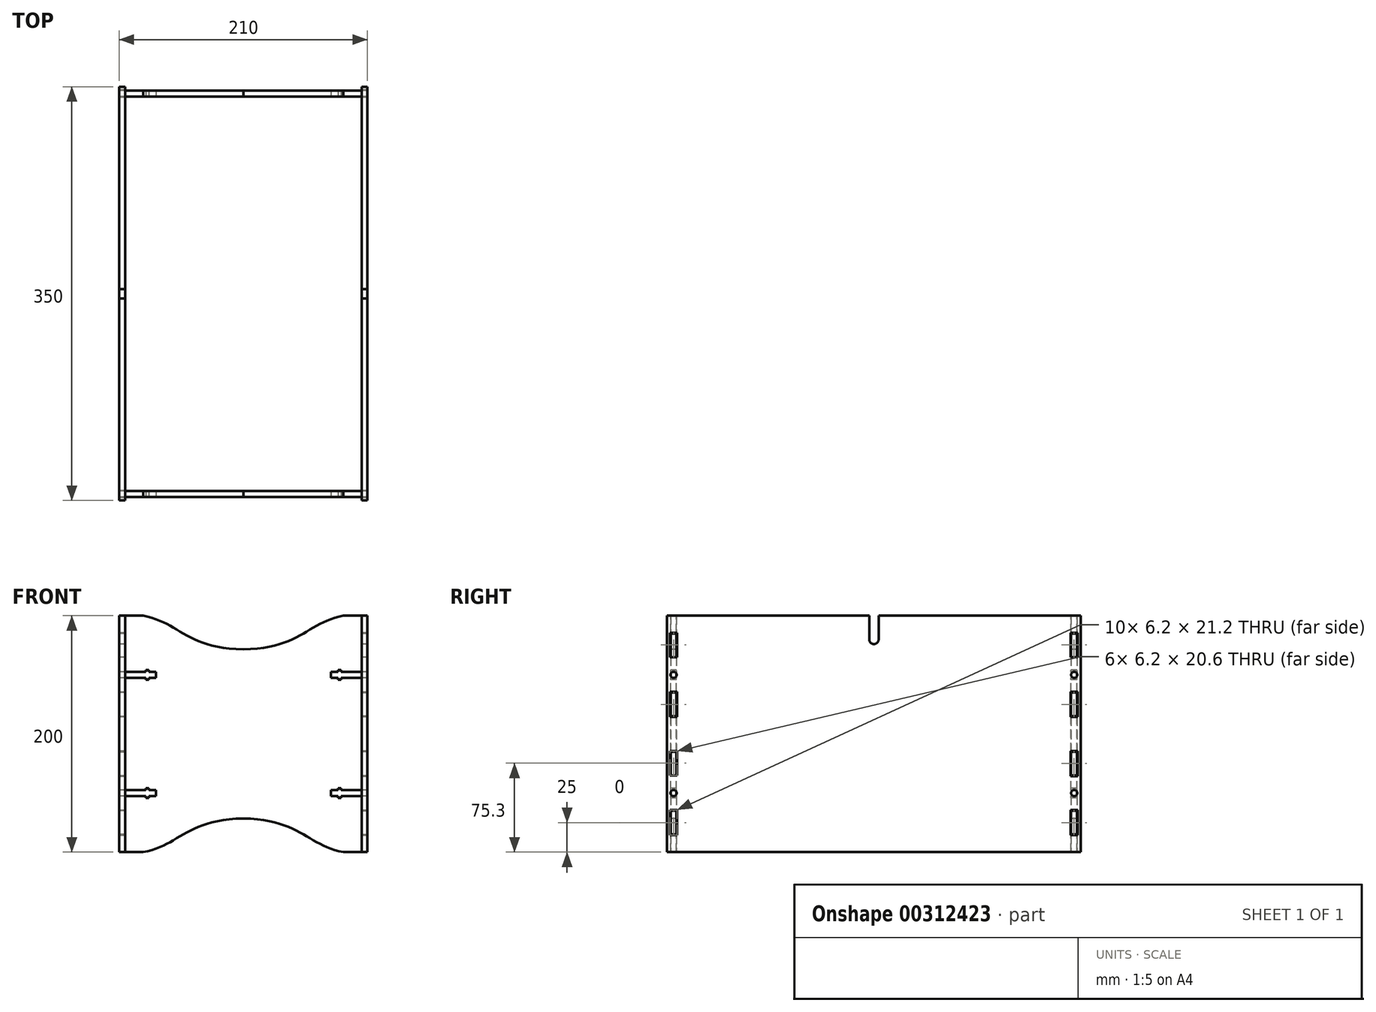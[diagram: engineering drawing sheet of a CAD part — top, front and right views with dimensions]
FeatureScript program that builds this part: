
annotation { "Feature Type Name" : "Feature", "Feature Type Description" : "" }
export const myFeature = defineFeature(function(context is Context, id is Id, definition is map)
    precondition{}
    {
        {
            var Q0;
            Q0=qCreatedBy(makeId("Right.planeOp"),FACE);
            var sketch = newSketch(context, id + "F0", { "sketchPlane" : qUnion([Q0])});
            skLineSegment(sketch, "E0.bottom", {"start": v(175, -100) * mm, "end": v(-175, -100) * mm});
            skLineSegment(sketch, "E0.top", {"start": v(175, 100) * mm, "end": v(4, 100) * mm});
            skLineSegment(sketch, "E0.left", {"start": v(175, -100) * mm, "end": v(175, 100) * mm});
            skLineSegment(sketch, "E0.right", {"start": v(-175, -100) * mm, "end": v(-175, 100) * mm});
            skPoint(sketch, "E0.middle", {"position": v(0, 0) * mm});
            skLineSegment(sketch, "E1", {"start": v(0, 80) * mm, "end": v(0, -100) * mm, "construction": true});
            skLineSegment(sketch, "E2", {"start": v(-175, 0) * mm, "end": v(175, 0) * mm, "construction": true});
            skLineSegment(sketch, "E3.trimOffspring", {"start": v(-4, 100) * mm, "end": v(-175, 100) * mm});
            skLineSegment(sketch, "E4", {"start": v(-172, 100) * mm, "end": v(-172, 85) * mm, "construction": true});
            skLineSegment(sketch, "E5", {"start": v(-166.8, 65) * mm, "end": v(-166.8, 35) * mm, "construction": true});
            skLineSegment(sketch, "E6.bottom", {"start": v(-172, 85) * mm, "end": v(-166.8, 85) * mm});
            skLineSegment(sketch, "E6.top", {"start": v(-172, 65) * mm, "end": v(-166.8, 65) * mm});
            skLineSegment(sketch, "E6.left", {"start": v(-172, 85) * mm, "end": v(-172, 65) * mm});
            skLineSegment(sketch, "E6.right", {"start": v(-166.8, 85) * mm, "end": v(-166.8, 65) * mm});
            skLineSegment(sketch, "E7.bottom", {"start": v(-172, 35) * mm, "end": v(-166.8, 35) * mm});
            skLineSegment(sketch, "E7.top", {"start": v(-172, 15) * mm, "end": v(-166.8, 15) * mm});
            skLineSegment(sketch, "E7.left", {"start": v(-172, 35) * mm, "end": v(-172, 15) * mm});
            skLineSegment(sketch, "E7.right", {"start": v(-166.8, 35) * mm, "end": v(-166.8, 15) * mm});
            skLineSegment(sketch, "E8", {"start": v(-169.4, 65) * mm, "end": v(-169.4, 35) * mm, "construction": true});
            skPoint(sketch, "E9", {"position": v(-169.4, 50) * mm});
            skCircle(sketch, "E10", {"center": v(-169.4, 50) * mm, "radius": 2.6 * mm});
            skLineSegment(sketch, "E11.MirrorCS", {"start": v(-172, -85) * mm, "end": v(-166.8, -85) * mm});
            skPoint(sketch, "E12.orphan", {"position": v(-166.8, 100) * mm});
            skLineSegment(sketch, "E13.trimOffspring", {"start": v(-172, 65) * mm, "end": v(-172, 35) * mm, "construction": true});
            skLineSegment(sketch, "E14.MirrorCS", {"start": v(-166.8, -85) * mm, "end": v(-166.8, -65) * mm});
            skLineSegment(sketch, "E15.MirrorCS", {"start": v(-172, -85) * mm, "end": v(-172, -65) * mm});
            skLineSegment(sketch, "E16.MirrorCS", {"start": v(-172, -65) * mm, "end": v(-166.8, -65) * mm});
            skCircle(sketch, "E17.MirrorC", {"center": v(-169.4, -50) * mm, "radius": 2.6 * mm});
            skLineSegment(sketch, "E18.MirrorCS", {"start": v(-172, -35) * mm, "end": v(-166.8, -35) * mm});
            skLineSegment(sketch, "E19.MirrorCS", {"start": v(-172, -15) * mm, "end": v(-166.8, -15) * mm});
            skLineSegment(sketch, "E20.trimOffspring", {"start": v(-172, 0) * mm, "end": v(-172, -15) * mm, "construction": true});
            skLineSegment(sketch, "E21.trimOffspring", {"start": v(-166.8, 0) * mm, "end": v(-166.8, -15) * mm, "construction": true});
            skLineSegment(sketch, "E22.MirrorCS", {"start": v(-172, -35) * mm, "end": v(-172, -15) * mm});
            skLineSegment(sketch, "E23.MirrorCS", {"start": v(-166.8, -35) * mm, "end": v(-166.8, -15) * mm});
            skLineSegment(sketch, "E24.trimOffspring", {"start": v(-172, -35) * mm, "end": v(-172, -65) * mm, "construction": true});
            skLineSegment(sketch, "E25.trimOffspring", {"start": v(-166.8, -35) * mm, "end": v(-166.8, -65) * mm, "construction": true});
            skLineSegment(sketch, "E26.trimOffspring", {"start": v(-166.8, -85) * mm, "end": v(-166.8, -100) * mm, "construction": true});
            skLineSegment(sketch, "E27.trimOffspring", {"start": v(-172, -85) * mm, "end": v(-172, -100) * mm, "construction": true});
            skLineSegment(sketch, "E28.MirrorCS", {"start": v(172, 85) * mm, "end": v(172, 65) * mm});
            skLineSegment(sketch, "E29.MirrorCS", {"start": v(166.8, 85) * mm, "end": v(166.8, 65) * mm});
            skLineSegment(sketch, "E30.MirrorCS", {"start": v(172, 85) * mm, "end": v(166.8, 85) * mm});
            skLineSegment(sketch, "E31.MirrorCS", {"start": v(172, 65) * mm, "end": v(166.8, 65) * mm});
            skCircle(sketch, "E32.MirrorC", {"center": v(169.4, 50) * mm, "radius": 2.6 * mm});
            skLineSegment(sketch, "E33.MirrorCS", {"start": v(172, 35) * mm, "end": v(166.8, 35) * mm});
            skLineSegment(sketch, "E34.MirrorCS", {"start": v(166.8, 35) * mm, "end": v(166.8, 15) * mm});
            skLineSegment(sketch, "E35.MirrorCS", {"start": v(172, 35) * mm, "end": v(172, 15) * mm});
            skLineSegment(sketch, "E36.MirrorCS", {"start": v(172, 15) * mm, "end": v(166.8, 15) * mm});
            skLineSegment(sketch, "E37.MirrorCS", {"start": v(172, -15) * mm, "end": v(166.8, -15) * mm});
            skLineSegment(sketch, "E38.MirrorCS", {"start": v(166.8, -35) * mm, "end": v(166.8, -15) * mm});
            skLineSegment(sketch, "E39.MirrorCS", {"start": v(172, -35) * mm, "end": v(172, -15) * mm});
            skLineSegment(sketch, "E40.MirrorCS", {"start": v(172, -35) * mm, "end": v(166.8, -35) * mm});
            skCircle(sketch, "E41.MirrorC", {"center": v(169.4, -50) * mm, "radius": 2.6 * mm});
            skLineSegment(sketch, "E42.MirrorCS", {"start": v(172, -65) * mm, "end": v(166.8, -65) * mm});
            skLineSegment(sketch, "E43.MirrorCS", {"start": v(172, -85) * mm, "end": v(166.8, -85) * mm});
            skLineSegment(sketch, "E44.MirrorCS", {"start": v(166.8, -85) * mm, "end": v(166.8, -65) * mm});
            skLineSegment(sketch, "E45.MirrorCS", {"start": v(172, -85) * mm, "end": v(172, -65) * mm});
            skLineSegment(sketch, "E46.left", {"start": v(4, 100) * mm, "end": v(4, 80) * mm});
            skLineSegment(sketch, "E46.right", {"start": v(-4, 100) * mm, "end": v(-4, 80) * mm});
            skArc(sketch, "E47", {"start": v(-4, 80) * mm, "mid": v(0, 76) * mm, "end": v(4, 80) * mm});
            skSolve(sketch);
        }
        {
            var Q0;
            Q0 = qSketchRegion(id + "F0", true);
            extrude(context, id + "F1", {"entities" : qUnion([Q0]), "depth" : 5 * mm});
        }
        {
            var Q0;
            Q0=makeQuery(id+"F1.opExtrude","SWEPT_FACE",FACE,{"disambiguationData":[OSD([sQuery(id+"F0.wireOp",EDGE,"E29.MirrorCS")])]});
            var sketch = newSketch(context, id + "F2", { "sketchPlane" : qUnion([Q0])});
            skPoint(sketch, "E48.0", {"position": v(-5, 100) * mm});
            skLineSegment(sketch, "E49.bottom", {"start": v(0, 100) * mm, "end": v(15.34, 100) * mm});
            skLineSegment(sketch, "E49.top", {"start": v(0, -100) * mm, "end": v(15.34, -100) * mm});
            skLineSegment(sketch, "E49.left", {"start": v(-5, 85) * mm, "end": v(-5, 65) * mm});
            skLineSegment(sketch, "E49.right", {"start": v(200, 100) * mm, "end": v(200, 52.6) * mm});
            skLineSegment(sketch, "E50.bottom", {"start": v(0, 52.6) * mm, "end": v(17.4, 52.6) * mm});
            skLineSegment(sketch, "E50.top", {"start": v(0, 47.4) * mm, "end": v(17.4, 47.4) * mm});
            skLineSegment(sketch, "E50.right", {"start": v(26, 52.6) * mm, "end": v(26, 47.4) * mm});
            skLineSegment(sketch, "E51.bottom", {"start": v(20, 45.95) * mm, "end": v(17.4, 45.95) * mm});
            skLineSegment(sketch, "E51.top", {"start": v(20, 54.05) * mm, "end": v(17.4, 54.05) * mm});
            skLineSegment(sketch, "E51.left", {"start": v(20, 45.95) * mm, "end": v(20, 47.4) * mm});
            skLineSegment(sketch, "E51.right", {"start": v(17.4, 45.95) * mm, "end": v(17.4, 47.4) * mm});
            skPoint(sketch, "E51.middle", {"position": v(18.7, 50) * mm});
            skPoint(sketch, "E51.middle.positionSnap0", {"position": v(26, 50) * mm});
            skPoint(sketch, "E51.centerSnap0", {"position": v(26, 50) * mm});
            skLineSegment(sketch, "E52.bottom", {"start": v(0, -47.4) * mm, "end": v(17.4, -47.4) * mm});
            skLineSegment(sketch, "E52.top", {"start": v(0, -52.6) * mm, "end": v(17.4, -52.6) * mm});
            skLineSegment(sketch, "E52.right", {"start": v(26, -47.4) * mm, "end": v(26, -52.6) * mm});
            skLineSegment(sketch, "E53.bottom", {"start": v(20, -54.05) * mm, "end": v(17.4, -54.05) * mm});
            skLineSegment(sketch, "E53.top", {"start": v(20, -45.95) * mm, "end": v(17.4, -45.95) * mm});
            skLineSegment(sketch, "E53.left", {"start": v(20, -54.05) * mm, "end": v(20, -52.6) * mm});
            skLineSegment(sketch, "E53.right", {"start": v(17.4, -54.05) * mm, "end": v(17.4, -52.6) * mm});
            skPoint(sketch, "E53.middle", {"position": v(18.7, -50) * mm});
            skPoint(sketch, "E53.middle.positionSnap0", {"position": v(26, -50) * mm});
            skPoint(sketch, "E53.centerSnap0", {"position": v(26, -50) * mm});
            skLineSegment(sketch, "E54.trimOffspring", {"start": v(17.4, 52.6) * mm, "end": v(17.4, 54.05) * mm});
            skLineSegment(sketch, "E55.trimOffspring", {"start": v(20, 52.6) * mm, "end": v(26, 52.6) * mm});
            skLineSegment(sketch, "E56.trimOffspring", {"start": v(20, 52.6) * mm, "end": v(20, 54.05) * mm});
            skLineSegment(sketch, "E57.trimOffspring", {"start": v(20, 47.4) * mm, "end": v(26, 47.4) * mm});
            skLineSegment(sketch, "E58.trimOffspring", {"start": v(20, -47.4) * mm, "end": v(26, -47.4) * mm});
            skLineSegment(sketch, "E59.trimOffspring", {"start": v(20, -52.6) * mm, "end": v(26, -52.6) * mm});
            skLineSegment(sketch, "E60.trimOffspring", {"start": v(17.4, -47.4) * mm, "end": v(17.4, -45.95) * mm});
            skLineSegment(sketch, "E61.trimOffspring", {"start": v(20, -47.4) * mm, "end": v(20, -45.95) * mm});
            skLineSegment(sketch, "E62.0", {"start": v(0, 85) * mm, "end": v(0, 65) * mm, "construction": true});
            skLineSegment(sketch, "E62.1", {"start": v(0, 35) * mm, "end": v(0, 15) * mm, "construction": true});
            skLineSegment(sketch, "E62.2", {"start": v(0, -35) * mm, "end": v(0, -15) * mm, "construction": true});
            skLineSegment(sketch, "E62.3", {"start": v(0, -85) * mm, "end": v(0, -65) * mm, "construction": true});
            skLineSegment(sketch, "E63.bottom", {"start": v(0, 85) * mm, "end": v(-5, 85) * mm});
            skLineSegment(sketch, "E63.left", {"start": v(0, 85) * mm, "end": v(0, 100) * mm});
            skLineSegment(sketch, "E64.bottom", {"start": v(0, 65) * mm, "end": v(-5, 65) * mm});
            skLineSegment(sketch, "E64.top", {"start": v(0, 35) * mm, "end": v(-5, 35) * mm});
            skLineSegment(sketch, "E64.left", {"start": v(0, 65) * mm, "end": v(0, 52.6) * mm});
            skLineSegment(sketch, "E65.bottom", {"start": v(0, 15) * mm, "end": v(0, 15) * mm});
            skLineSegment(sketch, "E65.top", {"start": v(0, -15) * mm, "end": v(0, -15) * mm});
            skLineSegment(sketch, "E65.left", {"start": v(0, 15) * mm, "end": v(0, -15) * mm});
            skLineSegment(sketch, "E65.right", {"start": v(0, 15) * mm, "end": v(0, -15) * mm});
            skLineSegment(sketch, "E66.bottom", {"start": v(-5, -15) * mm, "end": v(0, -15) * mm});
            skLineSegment(sketch, "E66.top", {"start": v(-5, 15) * mm, "end": v(0, 15) * mm});
            skLineSegment(sketch, "E66.right", {"start": v(0, -15) * mm, "end": v(0, 15) * mm});
            skLineSegment(sketch, "E67", {"start": v(0, -35) * mm, "end": v(-5, -35) * mm});
            skLineSegment(sketch, "E68", {"start": v(0, -85) * mm, "end": v(-5, -85) * mm});
            skLineSegment(sketch, "E69", {"start": v(0, -65) * mm, "end": v(-5, -65) * mm});
            skLineSegment(sketch, "E70.trimOffspring", {"start": v(-5, -15) * mm, "end": v(-5, -35) * mm});
            skLineSegment(sketch, "E71.trimOffspring", {"start": v(-5, -65) * mm, "end": v(-5, -85) * mm});
            skLineSegment(sketch, "E72", {"start": v(0, -85) * mm, "end": v(0, -100) * mm});
            skLineSegment(sketch, "E73", {"start": v(0, -52.6) * mm, "end": v(0, -65) * mm});
            skLineSegment(sketch, "E74", {"start": v(0, -47.4) * mm, "end": v(0, -35) * mm});
            skLineSegment(sketch, "E75", {"start": v(0, 35) * mm, "end": v(0, 47.4) * mm});
            skLineSegment(sketch, "E76", {"start": v(0, 52.6) * mm, "end": v(0, 65) * mm});
            skLineSegment(sketch, "E77.trimOffspring", {"start": v(0, 47.4) * mm, "end": v(0, 35) * mm});
            skLineSegment(sketch, "E78", {"start": v(-5, 65) * mm, "end": v(0, 65) * mm});
            skLineSegment(sketch, "E79.trimOffspring", {"start": v(-5, 35) * mm, "end": v(-5, 15) * mm});
            skLineSegment(sketch, "E80", {"start": v(100, 100) * mm, "end": v(100, -100) * mm, "construction": true});
            skLineSegment(sketch, "E81.MirrorCS", {"start": v(180, 54.05) * mm, "end": v(182.6, 54.05) * mm});
            skLineSegment(sketch, "E82.MirrorCS", {"start": v(205, 65) * mm, "end": v(200, 65) * mm});
            skLineSegment(sketch, "E83.MirrorCS", {"start": v(180, -45.95) * mm, "end": v(182.6, -45.95) * mm});
            skLineSegment(sketch, "E84.MirrorCS", {"start": v(182.6, -47.4) * mm, "end": v(182.6, -45.95) * mm});
            skLineSegment(sketch, "E85.MirrorCS", {"start": v(180, 52.6) * mm, "end": v(180, 54.05) * mm});
            skLineSegment(sketch, "E86.MirrorCS", {"start": v(182.6, 52.6) * mm, "end": v(182.6, 54.05) * mm});
            skLineSegment(sketch, "E87.MirrorCS", {"start": v(180, -47.4) * mm, "end": v(180, -45.95) * mm});
            skLineSegment(sketch, "E88.MirrorCS", {"start": v(180, -47.4) * mm, "end": v(174, -47.4) * mm});
            skLineSegment(sketch, "E89.MirrorCS", {"start": v(182.6, -54.05) * mm, "end": v(182.6, -52.6) * mm});
            skLineSegment(sketch, "E90.MirrorCS", {"start": v(180, -54.05) * mm, "end": v(182.6, -54.05) * mm});
            skLineSegment(sketch, "E91.MirrorCS", {"start": v(180, -54.05) * mm, "end": v(180, -52.6) * mm});
            skLineSegment(sketch, "E92.MirrorCS", {"start": v(200, 65) * mm, "end": v(205, 65) * mm});
            skLineSegment(sketch, "E93.MirrorCS", {"start": v(180, 52.6) * mm, "end": v(174, 52.6) * mm});
            skLineSegment(sketch, "E94.MirrorCS", {"start": v(200, 85) * mm, "end": v(205, 85) * mm});
            skLineSegment(sketch, "E95.MirrorCS", {"start": v(180, 45.95) * mm, "end": v(182.6, 45.95) * mm});
            skLineSegment(sketch, "E96.MirrorCS", {"start": v(174, 52.6) * mm, "end": v(174, 47.4) * mm});
            skLineSegment(sketch, "E97.MirrorCS", {"start": v(174, -47.4) * mm, "end": v(174, -52.6) * mm});
            skLineSegment(sketch, "E98.MirrorCS", {"start": v(180, -52.6) * mm, "end": v(174, -52.6) * mm});
            skLineSegment(sketch, "E99.MirrorCS", {"start": v(182.6, 45.95) * mm, "end": v(182.6, 47.4) * mm});
            skLineSegment(sketch, "E100.MirrorCS", {"start": v(180, 47.4) * mm, "end": v(174, 47.4) * mm});
            skLineSegment(sketch, "E101.MirrorCS", {"start": v(180, 45.95) * mm, "end": v(180, 47.4) * mm});
            skLineSegment(sketch, "E102.MirrorCS", {"start": v(205, -15) * mm, "end": v(200, -15) * mm});
            skLineSegment(sketch, "E103.MirrorCS", {"start": v(200, -15) * mm, "end": v(200, 15) * mm});
            skLineSegment(sketch, "E104.MirrorCS", {"start": v(205, 15) * mm, "end": v(200, 15) * mm});
            skLineSegment(sketch, "E105.MirrorCS", {"start": v(200, -35) * mm, "end": v(205, -35) * mm});
            skLineSegment(sketch, "E106.MirrorCS", {"start": v(200, 35) * mm, "end": v(205, 35) * mm});
            skLineSegment(sketch, "E107.MirrorCS", {"start": v(200, -65) * mm, "end": v(205, -65) * mm});
            skLineSegment(sketch, "E108.MirrorCS", {"start": v(200, -85) * mm, "end": v(205, -85) * mm});
            skLineSegment(sketch, "E109.MirrorCS", {"start": v(200, 52.6) * mm, "end": v(200, 65) * mm});
            skLineSegment(sketch, "E110.MirrorCS", {"start": v(200, 35) * mm, "end": v(200, 47.4) * mm});
            skPoint(sketch, "E111.MirrorP", {"position": v(174, 50) * mm});
            skLineSegment(sketch, "E112.MirrorCS", {"start": v(205, 85) * mm, "end": v(205, 65) * mm});
            skLineSegment(sketch, "E113.MirrorCS", {"start": v(200, 15) * mm, "end": v(200, -15) * mm});
            skPoint(sketch, "E114.MirrorP", {"position": v(174, -50) * mm});
            skLineSegment(sketch, "E115.MirrorCS", {"start": v(200, -15) * mm, "end": v(200, -15) * mm});
            skLineSegment(sketch, "E116.MirrorCS", {"start": v(200, 85) * mm, "end": v(200, 100) * mm});
            skPoint(sketch, "E117.MirrorP", {"position": v(205, 100) * mm});
            skLineSegment(sketch, "E118.MirrorCS", {"start": v(200, 52.6) * mm, "end": v(182.6, 52.6) * mm});
            skLineSegment(sketch, "E119.MirrorCS", {"start": v(200, 47.4) * mm, "end": v(182.6, 47.4) * mm});
            skLineSegment(sketch, "E120.MirrorCS", {"start": v(200, -47.4) * mm, "end": v(200, -35) * mm});
            skLineSegment(sketch, "E121.MirrorCS", {"start": v(200, -52.6) * mm, "end": v(182.6, -52.6) * mm});
            skLineSegment(sketch, "E122.MirrorCS", {"start": v(205, -15) * mm, "end": v(205, -35) * mm});
            skLineSegment(sketch, "E123.MirrorCS", {"start": v(200, 47.4) * mm, "end": v(200, 35) * mm});
            skLineSegment(sketch, "E124.MirrorCS", {"start": v(200, -85) * mm, "end": v(200, -100) * mm});
            skPoint(sketch, "E125.MirrorP", {"position": v(181.3, -50) * mm});
            skPoint(sketch, "E126.MirrorP", {"position": v(181.3, 50) * mm});
            skLineSegment(sketch, "E127.MirrorCS", {"start": v(200, 15) * mm, "end": v(200, 15) * mm});
            skLineSegment(sketch, "E128.MirrorCS", {"start": v(200, -47.4) * mm, "end": v(182.6, -47.4) * mm});
            skLineSegment(sketch, "E129.MirrorCS", {"start": v(200, -52.6) * mm, "end": v(200, -65) * mm});
            skLineSegment(sketch, "E130.MirrorCS", {"start": v(200, 65) * mm, "end": v(200, 52.6) * mm});
            skLineSegment(sketch, "E131.MirrorCS", {"start": v(205, 35) * mm, "end": v(205, 15) * mm});
            skLineSegment(sketch, "E132.MirrorCS", {"start": v(205, -65) * mm, "end": v(205, -85) * mm});
            skLineSegment(sketch, "E133.MirrorCS", {"start": v(200, 85) * mm, "end": v(200, 65) * mm, "construction": true});
            skFitSpline(sketch, "E134", {"points": [v(15.34, 100) * mm, v(100, 71.5) * mm], "startDerivative": vector(91.37, -16.34) * mm, "endDerivative": vector(146.95, -3.2) * mm});
            skFitSpline(sketch, "E135.MirrorCS", {"points": [v(184.66, 100) * mm, v(100, 71.5) * mm], "startDerivative": vector(-91.37, -16.34) * mm, "endDerivative": vector(-146.95, -3.2) * mm});
            skLineSegment(sketch, "E136.trimOffspring", {"start": v(184.66, 100) * mm, "end": v(200, 100) * mm});
            skLineSegment(sketch, "E137", {"start": v(100, 0) * mm, "end": v(200, 0) * mm, "construction": true});
            skFitSpline(sketch, "E138.MirrorCS", {"points": [v(184.66, -100) * mm, v(100, -71.5) * mm], "startDerivative": vector(-91.37, 16.34) * mm, "endDerivative": vector(-146.95, 3.2) * mm});
            skFitSpline(sketch, "E139.MirrorCS", {"points": [v(15.34, -100) * mm, v(100, -71.5) * mm], "startDerivative": vector(91.37, 16.34) * mm, "endDerivative": vector(146.95, 3.2) * mm});
            skLineSegment(sketch, "E140.trimOffspring", {"start": v(184.66, -100) * mm, "end": v(200, -100) * mm});
            skLineSegment(sketch, "E141.trimOffspring", {"start": v(200, 47.4) * mm, "end": v(200, -47.4) * mm});
            skLineSegment(sketch, "E142.trimOffspring", {"start": v(200, -52.6) * mm, "end": v(200, -100) * mm});
            skSolve(sketch);
        }
        {
            var Q0;
            Q0 = qSketchRegion(id + "F2", true);
            extrude(context, id + "F3", {"entities" : qUnion([Q0]), "depth" : 5 * mm});
        }
        {
            var Q0;
            Q0=makeQuery(id+"F3.opExtrude","SWEPT_BODY",BODY,{"disambiguationData":[OSD([sQuery(id+"F2.wireOp",EDGE,"E49.bottom"),sQuery(id+"F2.wireOp",EDGE,"E49.top"),sQuery(id+"F2.wireOp",EDGE,"E50.bottom"),sQuery(id+"F2.wireOp",EDGE,"E50.top"),sQuery(id+"F2.wireOp",EDGE,"E50.right"),sQuery(id+"F2.wireOp",EDGE,"E51.bottom"),sQuery(id+"F2.wireOp",EDGE,"E51.top"),sQuery(id+"F2.wireOp",EDGE,"E51.left"),sQuery(id+"F2.wireOp",EDGE,"E51.right"),sQuery(id+"F2.wireOp",EDGE,"E52.bottom"),sQuery(id+"F2.wireOp",EDGE,"E52.top"),sQuery(id+"F2.wireOp",EDGE,"E52.right"),sQuery(id+"F2.wireOp",EDGE,"E53.bottom"),sQuery(id+"F2.wireOp",EDGE,"E53.top"),sQuery(id+"F2.wireOp",EDGE,"E53.left"),sQuery(id+"F2.wireOp",EDGE,"E53.right"),sQuery(id+"F2.wireOp",EDGE,"E54.trimOffspring"),sQuery(id+"F2.wireOp",EDGE,"E55.trimOffspring"),sQuery(id+"F2.wireOp",EDGE,"E56.trimOffspring"),sQuery(id+"F2.wireOp",EDGE,"E57.trimOffspring"),sQuery(id+"F2.wireOp",EDGE,"E58.trimOffspring"),sQuery(id+"F2.wireOp",EDGE,"E59.trimOffspring"),sQuery(id+"F2.wireOp",EDGE,"E60.trimOffspring"),sQuery(id+"F2.wireOp",EDGE,"E61.trimOffspring"),sQuery(id+"F2.wireOp",EDGE,"E63.bottom"),sQuery(id+"F2.wireOp",EDGE,"E63.left"),sQuery(id+"F2.wireOp",EDGE,"E64.top"),sQuery(id+"F2.wireOp",EDGE,"E66.bottom"),sQuery(id+"F2.wireOp",EDGE,"E66.top"),sQuery(id+"F2.wireOp",EDGE,"E66.right"),sQuery(id+"F2.wireOp",EDGE,"E67"),sQuery(id+"F2.wireOp",EDGE,"E68"),sQuery(id+"F2.wireOp",EDGE,"E69"),sQuery(id+"F2.wireOp",EDGE,"E70.trimOffspring"),sQuery(id+"F2.wireOp",EDGE,"E71.trimOffspring"),sQuery(id+"F2.wireOp",EDGE,"E72"),sQuery(id+"F2.wireOp",EDGE,"E73"),sQuery(id+"F2.wireOp",EDGE,"E74"),sQuery(id+"F2.wireOp",EDGE,"E76"),sQuery(id+"F2.wireOp",EDGE,"E77.trimOffspring"),sQuery(id+"F2.wireOp",EDGE,"E49.left"),sQuery(id+"F2.wireOp",EDGE,"E78"),sQuery(id+"F2.wireOp",EDGE,"E79.trimOffspring"),sQuery(id+"F2.wireOp",EDGE,"E81.MirrorCS"),sQuery(id+"F2.wireOp",EDGE,"E83.MirrorCS"),sQuery(id+"F2.wireOp",EDGE,"E84.MirrorCS"),sQuery(id+"F2.wireOp",EDGE,"E85.MirrorCS"),sQuery(id+"F2.wireOp",EDGE,"E86.MirrorCS"),sQuery(id+"F2.wireOp",EDGE,"E87.MirrorCS"),sQuery(id+"F2.wireOp",EDGE,"E88.MirrorCS"),sQuery(id+"F2.wireOp",EDGE,"E89.MirrorCS"),sQuery(id+"F2.wireOp",EDGE,"E90.MirrorCS"),sQuery(id+"F2.wireOp",EDGE,"E91.MirrorCS"),sQuery(id+"F2.wireOp",EDGE,"E92.MirrorCS"),sQuery(id+"F2.wireOp",EDGE,"E93.MirrorCS"),sQuery(id+"F2.wireOp",EDGE,"E94.MirrorCS"),sQuery(id+"F2.wireOp",EDGE,"E95.MirrorCS"),sQuery(id+"F2.wireOp",EDGE,"E96.MirrorCS"),sQuery(id+"F2.wireOp",EDGE,"E97.MirrorCS"),sQuery(id+"F2.wireOp",EDGE,"E98.MirrorCS"),sQuery(id+"F2.wireOp",EDGE,"E99.MirrorCS"),sQuery(id+"F2.wireOp",EDGE,"E100.MirrorCS"),sQuery(id+"F2.wireOp",EDGE,"E101.MirrorCS"),sQuery(id+"F2.wireOp",EDGE,"E102.MirrorCS"),sQuery(id+"F2.wireOp",EDGE,"E104.MirrorCS"),sQuery(id+"F2.wireOp",EDGE,"E105.MirrorCS"),sQuery(id+"F2.wireOp",EDGE,"E106.MirrorCS"),sQuery(id+"F2.wireOp",EDGE,"E107.MirrorCS"),sQuery(id+"F2.wireOp",EDGE,"E108.MirrorCS"),sQuery(id+"F2.wireOp",EDGE,"E116.MirrorCS"),sQuery(id+"F2.wireOp",EDGE,"E118.MirrorCS"),sQuery(id+"F2.wireOp",EDGE,"E119.MirrorCS"),sQuery(id+"F2.wireOp",EDGE,"E121.MirrorCS"),sQuery(id+"F2.wireOp",EDGE,"E122.MirrorCS"),sQuery(id+"F2.wireOp",EDGE,"E128.MirrorCS"),sQuery(id+"F2.wireOp",EDGE,"E112.MirrorCS"),sQuery(id+"F2.wireOp",EDGE,"E130.MirrorCS"),sQuery(id+"F2.wireOp",EDGE,"E131.MirrorCS"),sQuery(id+"F2.wireOp",EDGE,"E132.MirrorCS"),sQuery(id+"F2.wireOp",EDGE,"E134"),sQuery(id+"F2.wireOp",EDGE,"E135.MirrorCS"),sQuery(id+"F2.wireOp",EDGE,"E136.trimOffspring"),sQuery(id+"F2.wireOp",EDGE,"E138.MirrorCS"),sQuery(id+"F2.wireOp",EDGE,"E139.MirrorCS"),sQuery(id+"F2.wireOp",EDGE,"E140.trimOffspring"),sQuery(id+"F2.wireOp",EDGE,"E141.trimOffspring"),sQuery(id+"F2.wireOp",EDGE,"E142.trimOffspring")])]});
            var Q1;
            Q1=makeQuery(id+"F1.opExtrude","SWEPT_BODY",BODY,{"disambiguationData":[OSD([sQuery(id+"F0.wireOp",EDGE,"E0.bottom"),sQuery(id+"F0.wireOp",EDGE,"E0.top"),sQuery(id+"F0.wireOp",EDGE,"E0.left"),sQuery(id+"F0.wireOp",EDGE,"E0.right"),sQuery(id+"F0.wireOp",EDGE,"E3.trimOffspring"),sQuery(id+"F0.wireOp",EDGE,"E6.bottom"),sQuery(id+"F0.wireOp",EDGE,"E6.top"),sQuery(id+"F0.wireOp",EDGE,"E6.left"),sQuery(id+"F0.wireOp",EDGE,"E6.right"),sQuery(id+"F0.wireOp",EDGE,"E7.bottom"),sQuery(id+"F0.wireOp",EDGE,"E7.top"),sQuery(id+"F0.wireOp",EDGE,"E7.left"),sQuery(id+"F0.wireOp",EDGE,"E7.right"),sQuery(id+"F0.wireOp",EDGE,"E10"),sQuery(id+"F0.wireOp",EDGE,"E14.MirrorCS"),sQuery(id+"F0.wireOp",EDGE,"E15.MirrorCS"),sQuery(id+"F0.wireOp",EDGE,"E11.MirrorCS"),sQuery(id+"F0.wireOp",EDGE,"E16.MirrorCS"),sQuery(id+"F0.wireOp",EDGE,"E17.MirrorC"),sQuery(id+"F0.wireOp",EDGE,"E18.MirrorCS"),sQuery(id+"F0.wireOp",EDGE,"E19.MirrorCS"),sQuery(id+"F0.wireOp",EDGE,"E22.MirrorCS"),sQuery(id+"F0.wireOp",EDGE,"E23.MirrorCS"),sQuery(id+"F0.wireOp",EDGE,"E28.MirrorCS"),sQuery(id+"F0.wireOp",EDGE,"E29.MirrorCS"),sQuery(id+"F0.wireOp",EDGE,"E30.MirrorCS"),sQuery(id+"F0.wireOp",EDGE,"E31.MirrorCS"),sQuery(id+"F0.wireOp",EDGE,"E32.MirrorC"),sQuery(id+"F0.wireOp",EDGE,"E33.MirrorCS"),sQuery(id+"F0.wireOp",EDGE,"E34.MirrorCS"),sQuery(id+"F0.wireOp",EDGE,"E35.MirrorCS"),sQuery(id+"F0.wireOp",EDGE,"E36.MirrorCS"),sQuery(id+"F0.wireOp",EDGE,"E37.MirrorCS"),sQuery(id+"F0.wireOp",EDGE,"E38.MirrorCS"),sQuery(id+"F0.wireOp",EDGE,"E39.MirrorCS"),sQuery(id+"F0.wireOp",EDGE,"E40.MirrorCS"),sQuery(id+"F0.wireOp",EDGE,"E41.MirrorC"),sQuery(id+"F0.wireOp",EDGE,"E42.MirrorCS"),sQuery(id+"F0.wireOp",EDGE,"E43.MirrorCS"),sQuery(id+"F0.wireOp",EDGE,"E44.MirrorCS"),sQuery(id+"F0.wireOp",EDGE,"E45.MirrorCS"),sQuery(id+"F0.wireOp",EDGE,"E46.left"),sQuery(id+"F0.wireOp",EDGE,"E46.right"),sQuery(id+"F0.wireOp",EDGE,"E47")])]});
            var Q2;
            Q2=makeQuery(id+"F3.opExtrude","CAP_FACE",FACE,{"disambiguationData":[OSD([sQuery(id+"F2.wireOp",EDGE,"E49.bottom"),sQuery(id+"F2.wireOp",EDGE,"E49.top"),sQuery(id+"F2.wireOp",EDGE,"E50.bottom"),sQuery(id+"F2.wireOp",EDGE,"E50.top"),sQuery(id+"F2.wireOp",EDGE,"E50.right"),sQuery(id+"F2.wireOp",EDGE,"E51.bottom"),sQuery(id+"F2.wireOp",EDGE,"E51.top"),sQuery(id+"F2.wireOp",EDGE,"E51.left"),sQuery(id+"F2.wireOp",EDGE,"E51.right"),sQuery(id+"F2.wireOp",EDGE,"E52.bottom"),sQuery(id+"F2.wireOp",EDGE,"E52.top"),sQuery(id+"F2.wireOp",EDGE,"E52.right"),sQuery(id+"F2.wireOp",EDGE,"E53.bottom"),sQuery(id+"F2.wireOp",EDGE,"E53.top"),sQuery(id+"F2.wireOp",EDGE,"E53.left"),sQuery(id+"F2.wireOp",EDGE,"E53.right"),sQuery(id+"F2.wireOp",EDGE,"E54.trimOffspring"),sQuery(id+"F2.wireOp",EDGE,"E55.trimOffspring"),sQuery(id+"F2.wireOp",EDGE,"E56.trimOffspring"),sQuery(id+"F2.wireOp",EDGE,"E57.trimOffspring"),sQuery(id+"F2.wireOp",EDGE,"E58.trimOffspring"),sQuery(id+"F2.wireOp",EDGE,"E59.trimOffspring"),sQuery(id+"F2.wireOp",EDGE,"E60.trimOffspring"),sQuery(id+"F2.wireOp",EDGE,"E61.trimOffspring"),sQuery(id+"F2.wireOp",EDGE,"E63.bottom"),sQuery(id+"F2.wireOp",EDGE,"E63.left"),sQuery(id+"F2.wireOp",EDGE,"E64.top"),sQuery(id+"F2.wireOp",EDGE,"E66.bottom"),sQuery(id+"F2.wireOp",EDGE,"E66.top"),sQuery(id+"F2.wireOp",EDGE,"E66.right"),sQuery(id+"F2.wireOp",EDGE,"E67"),sQuery(id+"F2.wireOp",EDGE,"E68"),sQuery(id+"F2.wireOp",EDGE,"E69"),sQuery(id+"F2.wireOp",EDGE,"E70.trimOffspring"),sQuery(id+"F2.wireOp",EDGE,"E71.trimOffspring"),sQuery(id+"F2.wireOp",EDGE,"E72"),sQuery(id+"F2.wireOp",EDGE,"E73"),sQuery(id+"F2.wireOp",EDGE,"E74"),sQuery(id+"F2.wireOp",EDGE,"E76"),sQuery(id+"F2.wireOp",EDGE,"E77.trimOffspring"),sQuery(id+"F2.wireOp",EDGE,"E49.left"),sQuery(id+"F2.wireOp",EDGE,"E78"),sQuery(id+"F2.wireOp",EDGE,"E79.trimOffspring"),sQuery(id+"F2.wireOp",EDGE,"E81.MirrorCS"),sQuery(id+"F2.wireOp",EDGE,"E83.MirrorCS"),sQuery(id+"F2.wireOp",EDGE,"E84.MirrorCS"),sQuery(id+"F2.wireOp",EDGE,"E85.MirrorCS"),sQuery(id+"F2.wireOp",EDGE,"E86.MirrorCS"),sQuery(id+"F2.wireOp",EDGE,"E87.MirrorCS"),sQuery(id+"F2.wireOp",EDGE,"E88.MirrorCS"),sQuery(id+"F2.wireOp",EDGE,"E89.MirrorCS"),sQuery(id+"F2.wireOp",EDGE,"E90.MirrorCS"),sQuery(id+"F2.wireOp",EDGE,"E91.MirrorCS"),sQuery(id+"F2.wireOp",EDGE,"E92.MirrorCS"),sQuery(id+"F2.wireOp",EDGE,"E93.MirrorCS"),sQuery(id+"F2.wireOp",EDGE,"E94.MirrorCS"),sQuery(id+"F2.wireOp",EDGE,"E95.MirrorCS"),sQuery(id+"F2.wireOp",EDGE,"E96.MirrorCS"),sQuery(id+"F2.wireOp",EDGE,"E97.MirrorCS"),sQuery(id+"F2.wireOp",EDGE,"E98.MirrorCS"),sQuery(id+"F2.wireOp",EDGE,"E99.MirrorCS"),sQuery(id+"F2.wireOp",EDGE,"E100.MirrorCS"),sQuery(id+"F2.wireOp",EDGE,"E101.MirrorCS"),sQuery(id+"F2.wireOp",EDGE,"E102.MirrorCS"),sQuery(id+"F2.wireOp",EDGE,"E104.MirrorCS"),sQuery(id+"F2.wireOp",EDGE,"E105.MirrorCS"),sQuery(id+"F2.wireOp",EDGE,"E106.MirrorCS"),sQuery(id+"F2.wireOp",EDGE,"E107.MirrorCS"),sQuery(id+"F2.wireOp",EDGE,"E108.MirrorCS"),sQuery(id+"F2.wireOp",EDGE,"E116.MirrorCS"),sQuery(id+"F2.wireOp",EDGE,"E118.MirrorCS"),sQuery(id+"F2.wireOp",EDGE,"E119.MirrorCS"),sQuery(id+"F2.wireOp",EDGE,"E121.MirrorCS"),sQuery(id+"F2.wireOp",EDGE,"E122.MirrorCS"),sQuery(id+"F2.wireOp",EDGE,"E128.MirrorCS"),sQuery(id+"F2.wireOp",EDGE,"E112.MirrorCS"),sQuery(id+"F2.wireOp",EDGE,"E130.MirrorCS"),sQuery(id+"F2.wireOp",EDGE,"E131.MirrorCS"),sQuery(id+"F2.wireOp",EDGE,"E132.MirrorCS"),sQuery(id+"F2.wireOp",EDGE,"E134"),sQuery(id+"F2.wireOp",EDGE,"E135.MirrorCS"),sQuery(id+"F2.wireOp",EDGE,"E136.trimOffspring"),sQuery(id+"F2.wireOp",EDGE,"E138.MirrorCS"),sQuery(id+"F2.wireOp",EDGE,"E139.MirrorCS"),sQuery(id+"F2.wireOp",EDGE,"E140.trimOffspring"),sQuery(id+"F2.wireOp",EDGE,"E141.trimOffspring"),sQuery(id+"F2.wireOp",EDGE,"E142.trimOffspring")])],"isStart":false});
            var Q3;
            Q3=makeQuery(id+"F3.opExtrude","CAP_FACE",FACE,{"disambiguationData":[OSD([sQuery(id+"F2.wireOp",EDGE,"E49.bottom"),sQuery(id+"F2.wireOp",EDGE,"E49.top"),sQuery(id+"F2.wireOp",EDGE,"E50.bottom"),sQuery(id+"F2.wireOp",EDGE,"E50.top"),sQuery(id+"F2.wireOp",EDGE,"E50.right"),sQuery(id+"F2.wireOp",EDGE,"E51.bottom"),sQuery(id+"F2.wireOp",EDGE,"E51.top"),sQuery(id+"F2.wireOp",EDGE,"E51.left"),sQuery(id+"F2.wireOp",EDGE,"E51.right"),sQuery(id+"F2.wireOp",EDGE,"E52.bottom"),sQuery(id+"F2.wireOp",EDGE,"E52.top"),sQuery(id+"F2.wireOp",EDGE,"E52.right"),sQuery(id+"F2.wireOp",EDGE,"E53.bottom"),sQuery(id+"F2.wireOp",EDGE,"E53.top"),sQuery(id+"F2.wireOp",EDGE,"E53.left"),sQuery(id+"F2.wireOp",EDGE,"E53.right"),sQuery(id+"F2.wireOp",EDGE,"E54.trimOffspring"),sQuery(id+"F2.wireOp",EDGE,"E55.trimOffspring"),sQuery(id+"F2.wireOp",EDGE,"E56.trimOffspring"),sQuery(id+"F2.wireOp",EDGE,"E57.trimOffspring"),sQuery(id+"F2.wireOp",EDGE,"E58.trimOffspring"),sQuery(id+"F2.wireOp",EDGE,"E59.trimOffspring"),sQuery(id+"F2.wireOp",EDGE,"E60.trimOffspring"),sQuery(id+"F2.wireOp",EDGE,"E61.trimOffspring"),sQuery(id+"F2.wireOp",EDGE,"E63.bottom"),sQuery(id+"F2.wireOp",EDGE,"E63.left"),sQuery(id+"F2.wireOp",EDGE,"E64.top"),sQuery(id+"F2.wireOp",EDGE,"E66.bottom"),sQuery(id+"F2.wireOp",EDGE,"E66.top"),sQuery(id+"F2.wireOp",EDGE,"E66.right"),sQuery(id+"F2.wireOp",EDGE,"E67"),sQuery(id+"F2.wireOp",EDGE,"E68"),sQuery(id+"F2.wireOp",EDGE,"E69"),sQuery(id+"F2.wireOp",EDGE,"E70.trimOffspring"),sQuery(id+"F2.wireOp",EDGE,"E71.trimOffspring"),sQuery(id+"F2.wireOp",EDGE,"E72"),sQuery(id+"F2.wireOp",EDGE,"E73"),sQuery(id+"F2.wireOp",EDGE,"E74"),sQuery(id+"F2.wireOp",EDGE,"E76"),sQuery(id+"F2.wireOp",EDGE,"E77.trimOffspring"),sQuery(id+"F2.wireOp",EDGE,"E49.left"),sQuery(id+"F2.wireOp",EDGE,"E78"),sQuery(id+"F2.wireOp",EDGE,"E79.trimOffspring"),sQuery(id+"F2.wireOp",EDGE,"E81.MirrorCS"),sQuery(id+"F2.wireOp",EDGE,"E83.MirrorCS"),sQuery(id+"F2.wireOp",EDGE,"E84.MirrorCS"),sQuery(id+"F2.wireOp",EDGE,"E85.MirrorCS"),sQuery(id+"F2.wireOp",EDGE,"E86.MirrorCS"),sQuery(id+"F2.wireOp",EDGE,"E87.MirrorCS"),sQuery(id+"F2.wireOp",EDGE,"E88.MirrorCS"),sQuery(id+"F2.wireOp",EDGE,"E89.MirrorCS"),sQuery(id+"F2.wireOp",EDGE,"E90.MirrorCS"),sQuery(id+"F2.wireOp",EDGE,"E91.MirrorCS"),sQuery(id+"F2.wireOp",EDGE,"E92.MirrorCS"),sQuery(id+"F2.wireOp",EDGE,"E93.MirrorCS"),sQuery(id+"F2.wireOp",EDGE,"E94.MirrorCS"),sQuery(id+"F2.wireOp",EDGE,"E95.MirrorCS"),sQuery(id+"F2.wireOp",EDGE,"E96.MirrorCS"),sQuery(id+"F2.wireOp",EDGE,"E97.MirrorCS"),sQuery(id+"F2.wireOp",EDGE,"E98.MirrorCS"),sQuery(id+"F2.wireOp",EDGE,"E99.MirrorCS"),sQuery(id+"F2.wireOp",EDGE,"E100.MirrorCS"),sQuery(id+"F2.wireOp",EDGE,"E101.MirrorCS"),sQuery(id+"F2.wireOp",EDGE,"E102.MirrorCS"),sQuery(id+"F2.wireOp",EDGE,"E104.MirrorCS"),sQuery(id+"F2.wireOp",EDGE,"E105.MirrorCS"),sQuery(id+"F2.wireOp",EDGE,"E106.MirrorCS"),sQuery(id+"F2.wireOp",EDGE,"E107.MirrorCS"),sQuery(id+"F2.wireOp",EDGE,"E108.MirrorCS"),sQuery(id+"F2.wireOp",EDGE,"E116.MirrorCS"),sQuery(id+"F2.wireOp",EDGE,"E118.MirrorCS"),sQuery(id+"F2.wireOp",EDGE,"E119.MirrorCS"),sQuery(id+"F2.wireOp",EDGE,"E121.MirrorCS"),sQuery(id+"F2.wireOp",EDGE,"E122.MirrorCS"),sQuery(id+"F2.wireOp",EDGE,"E128.MirrorCS"),sQuery(id+"F2.wireOp",EDGE,"E112.MirrorCS"),sQuery(id+"F2.wireOp",EDGE,"E130.MirrorCS"),sQuery(id+"F2.wireOp",EDGE,"E131.MirrorCS"),sQuery(id+"F2.wireOp",EDGE,"E132.MirrorCS"),sQuery(id+"F2.wireOp",EDGE,"E134"),sQuery(id+"F2.wireOp",EDGE,"E135.MirrorCS"),sQuery(id+"F2.wireOp",EDGE,"E136.trimOffspring"),sQuery(id+"F2.wireOp",EDGE,"E138.MirrorCS"),sQuery(id+"F2.wireOp",EDGE,"E139.MirrorCS"),sQuery(id+"F2.wireOp",EDGE,"E140.trimOffspring"),sQuery(id+"F2.wireOp",EDGE,"E141.trimOffspring"),sQuery(id+"F2.wireOp",EDGE,"E142.trimOffspring")])],"isStart":true});
            var Q4;
            Q4=makeQuery(id+"F3.opExtrude","SWEPT_FACE",FACE,{"disambiguationData":[OSD([sQuery(id+"F2.wireOp",EDGE,"E63.bottom")])]});
            var Q5;
            Q5=makeQuery(id+"F3.opExtrude","SWEPT_FACE",FACE,{"disambiguationData":[OSD([sQuery(id+"F2.wireOp",EDGE,"E78")])]});
            var Q6;
            Q6=makeQuery(id+"F3.opExtrude","SWEPT_FACE",FACE,{"disambiguationData":[OSD([sQuery(id+"F2.wireOp",EDGE,"E66.top")])]});
            var Q7;
            Q7=makeQuery(id+"F3.opExtrude","SWEPT_FACE",FACE,{"disambiguationData":[OSD([sQuery(id+"F2.wireOp",EDGE,"E64.top")])]});
            var Q8;
            Q8=makeQuery(id+"F3.opExtrude","SWEPT_FACE",FACE,{"disambiguationData":[OSD([sQuery(id+"F2.wireOp",EDGE,"E66.bottom")])]});
            var Q9;
            Q9=makeQuery(id+"F3.opExtrude","SWEPT_FACE",FACE,{"disambiguationData":[OSD([sQuery(id+"F2.wireOp",EDGE,"E67")])]});
            var Q10;
            Q10=makeQuery(id+"F3.opExtrude","SWEPT_FACE",FACE,{"disambiguationData":[OSD([sQuery(id+"F2.wireOp",EDGE,"E69")])]});
            var Q11;
            Q11=makeQuery(id+"F3.opExtrude","SWEPT_FACE",FACE,{"disambiguationData":[OSD([sQuery(id+"F2.wireOp",EDGE,"E68")])]});
            booleanBodies(context, id + "F4", {"operationType" : BooleanOperationType.SUBTRACTION, "tools" : qUnion([Q0]), "targets" : qUnion([Q1]), "offset" : true, "entitiesToOffset" : qUnion([Q2, Q3, Q4, Q5, Q6, Q7, Q8, Q9, Q10, Q11]), "offsetDistance" : 0.6 * mm, "keepTools" : true});
        }
        {
            var Q0;
            Q0=makeQuery(id+"F3.opExtrude","SWEPT_BODY",BODY,{"disambiguationData":[OSD([sQuery(id+"F2.wireOp",EDGE,"E49.bottom"),sQuery(id+"F2.wireOp",EDGE,"E49.top"),sQuery(id+"F2.wireOp",EDGE,"E50.bottom"),sQuery(id+"F2.wireOp",EDGE,"E50.top"),sQuery(id+"F2.wireOp",EDGE,"E50.right"),sQuery(id+"F2.wireOp",EDGE,"E51.bottom"),sQuery(id+"F2.wireOp",EDGE,"E51.top"),sQuery(id+"F2.wireOp",EDGE,"E51.left"),sQuery(id+"F2.wireOp",EDGE,"E51.right"),sQuery(id+"F2.wireOp",EDGE,"E52.bottom"),sQuery(id+"F2.wireOp",EDGE,"E52.top"),sQuery(id+"F2.wireOp",EDGE,"E52.right"),sQuery(id+"F2.wireOp",EDGE,"E53.bottom"),sQuery(id+"F2.wireOp",EDGE,"E53.top"),sQuery(id+"F2.wireOp",EDGE,"E53.left"),sQuery(id+"F2.wireOp",EDGE,"E53.right"),sQuery(id+"F2.wireOp",EDGE,"E54.trimOffspring"),sQuery(id+"F2.wireOp",EDGE,"E55.trimOffspring"),sQuery(id+"F2.wireOp",EDGE,"E56.trimOffspring"),sQuery(id+"F2.wireOp",EDGE,"E57.trimOffspring"),sQuery(id+"F2.wireOp",EDGE,"E58.trimOffspring"),sQuery(id+"F2.wireOp",EDGE,"E59.trimOffspring"),sQuery(id+"F2.wireOp",EDGE,"E60.trimOffspring"),sQuery(id+"F2.wireOp",EDGE,"E61.trimOffspring"),sQuery(id+"F2.wireOp",EDGE,"E63.bottom"),sQuery(id+"F2.wireOp",EDGE,"E63.left"),sQuery(id+"F2.wireOp",EDGE,"E64.top"),sQuery(id+"F2.wireOp",EDGE,"E66.bottom"),sQuery(id+"F2.wireOp",EDGE,"E66.top"),sQuery(id+"F2.wireOp",EDGE,"E66.right"),sQuery(id+"F2.wireOp",EDGE,"E67"),sQuery(id+"F2.wireOp",EDGE,"E68"),sQuery(id+"F2.wireOp",EDGE,"E69"),sQuery(id+"F2.wireOp",EDGE,"E70.trimOffspring"),sQuery(id+"F2.wireOp",EDGE,"E71.trimOffspring"),sQuery(id+"F2.wireOp",EDGE,"E72"),sQuery(id+"F2.wireOp",EDGE,"E73"),sQuery(id+"F2.wireOp",EDGE,"E74"),sQuery(id+"F2.wireOp",EDGE,"E76"),sQuery(id+"F2.wireOp",EDGE,"E77.trimOffspring"),sQuery(id+"F2.wireOp",EDGE,"E49.left"),sQuery(id+"F2.wireOp",EDGE,"E78"),sQuery(id+"F2.wireOp",EDGE,"E79.trimOffspring"),sQuery(id+"F2.wireOp",EDGE,"E81.MirrorCS"),sQuery(id+"F2.wireOp",EDGE,"E83.MirrorCS"),sQuery(id+"F2.wireOp",EDGE,"E84.MirrorCS"),sQuery(id+"F2.wireOp",EDGE,"E85.MirrorCS"),sQuery(id+"F2.wireOp",EDGE,"E86.MirrorCS"),sQuery(id+"F2.wireOp",EDGE,"E87.MirrorCS"),sQuery(id+"F2.wireOp",EDGE,"E88.MirrorCS"),sQuery(id+"F2.wireOp",EDGE,"E89.MirrorCS"),sQuery(id+"F2.wireOp",EDGE,"E90.MirrorCS"),sQuery(id+"F2.wireOp",EDGE,"E91.MirrorCS"),sQuery(id+"F2.wireOp",EDGE,"E92.MirrorCS"),sQuery(id+"F2.wireOp",EDGE,"E93.MirrorCS"),sQuery(id+"F2.wireOp",EDGE,"E94.MirrorCS"),sQuery(id+"F2.wireOp",EDGE,"E95.MirrorCS"),sQuery(id+"F2.wireOp",EDGE,"E96.MirrorCS"),sQuery(id+"F2.wireOp",EDGE,"E97.MirrorCS"),sQuery(id+"F2.wireOp",EDGE,"E98.MirrorCS"),sQuery(id+"F2.wireOp",EDGE,"E99.MirrorCS"),sQuery(id+"F2.wireOp",EDGE,"E100.MirrorCS"),sQuery(id+"F2.wireOp",EDGE,"E101.MirrorCS"),sQuery(id+"F2.wireOp",EDGE,"E102.MirrorCS"),sQuery(id+"F2.wireOp",EDGE,"E104.MirrorCS"),sQuery(id+"F2.wireOp",EDGE,"E105.MirrorCS"),sQuery(id+"F2.wireOp",EDGE,"E106.MirrorCS"),sQuery(id+"F2.wireOp",EDGE,"E107.MirrorCS"),sQuery(id+"F2.wireOp",EDGE,"E108.MirrorCS"),sQuery(id+"F2.wireOp",EDGE,"E116.MirrorCS"),sQuery(id+"F2.wireOp",EDGE,"E118.MirrorCS"),sQuery(id+"F2.wireOp",EDGE,"E119.MirrorCS"),sQuery(id+"F2.wireOp",EDGE,"E121.MirrorCS"),sQuery(id+"F2.wireOp",EDGE,"E122.MirrorCS"),sQuery(id+"F2.wireOp",EDGE,"E128.MirrorCS"),sQuery(id+"F2.wireOp",EDGE,"E112.MirrorCS"),sQuery(id+"F2.wireOp",EDGE,"E130.MirrorCS"),sQuery(id+"F2.wireOp",EDGE,"E131.MirrorCS"),sQuery(id+"F2.wireOp",EDGE,"E132.MirrorCS"),sQuery(id+"F2.wireOp",EDGE,"E134"),sQuery(id+"F2.wireOp",EDGE,"E135.MirrorCS"),sQuery(id+"F2.wireOp",EDGE,"E136.trimOffspring"),sQuery(id+"F2.wireOp",EDGE,"E138.MirrorCS"),sQuery(id+"F2.wireOp",EDGE,"E139.MirrorCS"),sQuery(id+"F2.wireOp",EDGE,"E140.trimOffspring"),sQuery(id+"F2.wireOp",EDGE,"E141.trimOffspring"),sQuery(id+"F2.wireOp",EDGE,"E142.trimOffspring")])]});
            transform(context, id + "F5", {"entities" : qUnion([Q0]), "transformType" : TransformType.TRANSLATION_3D, "dx" : 0 * mm, "dy" : -338.7 * mm, "dz" : 0 * mm, "makeCopy" : true});
        }
        {
            var Q0;
            Q0=makeQuery(id+"F5.opPattern","COPY",BODY,{"derivedFrom":makeQuery(id+"F3.opExtrude","SWEPT_BODY",BODY,{"disambiguationData":[OSD([sQuery(id+"F2.wireOp",EDGE,"E49.bottom"),sQuery(id+"F2.wireOp",EDGE,"E49.top"),sQuery(id+"F2.wireOp",EDGE,"E50.bottom"),sQuery(id+"F2.wireOp",EDGE,"E50.top"),sQuery(id+"F2.wireOp",EDGE,"E50.right"),sQuery(id+"F2.wireOp",EDGE,"E51.bottom"),sQuery(id+"F2.wireOp",EDGE,"E51.top"),sQuery(id+"F2.wireOp",EDGE,"E51.left"),sQuery(id+"F2.wireOp",EDGE,"E51.right"),sQuery(id+"F2.wireOp",EDGE,"E52.bottom"),sQuery(id+"F2.wireOp",EDGE,"E52.top"),sQuery(id+"F2.wireOp",EDGE,"E52.right"),sQuery(id+"F2.wireOp",EDGE,"E53.bottom"),sQuery(id+"F2.wireOp",EDGE,"E53.top"),sQuery(id+"F2.wireOp",EDGE,"E53.left"),sQuery(id+"F2.wireOp",EDGE,"E53.right"),sQuery(id+"F2.wireOp",EDGE,"E54.trimOffspring"),sQuery(id+"F2.wireOp",EDGE,"E55.trimOffspring"),sQuery(id+"F2.wireOp",EDGE,"E56.trimOffspring"),sQuery(id+"F2.wireOp",EDGE,"E57.trimOffspring"),sQuery(id+"F2.wireOp",EDGE,"E58.trimOffspring"),sQuery(id+"F2.wireOp",EDGE,"E59.trimOffspring"),sQuery(id+"F2.wireOp",EDGE,"E60.trimOffspring"),sQuery(id+"F2.wireOp",EDGE,"E61.trimOffspring"),sQuery(id+"F2.wireOp",EDGE,"E63.bottom"),sQuery(id+"F2.wireOp",EDGE,"E63.left"),sQuery(id+"F2.wireOp",EDGE,"E64.top"),sQuery(id+"F2.wireOp",EDGE,"E66.bottom"),sQuery(id+"F2.wireOp",EDGE,"E66.top"),sQuery(id+"F2.wireOp",EDGE,"E66.right"),sQuery(id+"F2.wireOp",EDGE,"E67"),sQuery(id+"F2.wireOp",EDGE,"E68"),sQuery(id+"F2.wireOp",EDGE,"E69"),sQuery(id+"F2.wireOp",EDGE,"E70.trimOffspring"),sQuery(id+"F2.wireOp",EDGE,"E71.trimOffspring"),sQuery(id+"F2.wireOp",EDGE,"E72"),sQuery(id+"F2.wireOp",EDGE,"E73"),sQuery(id+"F2.wireOp",EDGE,"E74"),sQuery(id+"F2.wireOp",EDGE,"E76"),sQuery(id+"F2.wireOp",EDGE,"E77.trimOffspring"),sQuery(id+"F2.wireOp",EDGE,"E49.left"),sQuery(id+"F2.wireOp",EDGE,"E78"),sQuery(id+"F2.wireOp",EDGE,"E79.trimOffspring"),sQuery(id+"F2.wireOp",EDGE,"E81.MirrorCS"),sQuery(id+"F2.wireOp",EDGE,"E83.MirrorCS"),sQuery(id+"F2.wireOp",EDGE,"E84.MirrorCS"),sQuery(id+"F2.wireOp",EDGE,"E85.MirrorCS"),sQuery(id+"F2.wireOp",EDGE,"E86.MirrorCS"),sQuery(id+"F2.wireOp",EDGE,"E87.MirrorCS"),sQuery(id+"F2.wireOp",EDGE,"E88.MirrorCS"),sQuery(id+"F2.wireOp",EDGE,"E89.MirrorCS"),sQuery(id+"F2.wireOp",EDGE,"E90.MirrorCS"),sQuery(id+"F2.wireOp",EDGE,"E91.MirrorCS"),sQuery(id+"F2.wireOp",EDGE,"E92.MirrorCS"),sQuery(id+"F2.wireOp",EDGE,"E93.MirrorCS"),sQuery(id+"F2.wireOp",EDGE,"E94.MirrorCS"),sQuery(id+"F2.wireOp",EDGE,"E95.MirrorCS"),sQuery(id+"F2.wireOp",EDGE,"E96.MirrorCS"),sQuery(id+"F2.wireOp",EDGE,"E97.MirrorCS"),sQuery(id+"F2.wireOp",EDGE,"E98.MirrorCS"),sQuery(id+"F2.wireOp",EDGE,"E99.MirrorCS"),sQuery(id+"F2.wireOp",EDGE,"E100.MirrorCS"),sQuery(id+"F2.wireOp",EDGE,"E101.MirrorCS"),sQuery(id+"F2.wireOp",EDGE,"E102.MirrorCS"),sQuery(id+"F2.wireOp",EDGE,"E104.MirrorCS"),sQuery(id+"F2.wireOp",EDGE,"E105.MirrorCS"),sQuery(id+"F2.wireOp",EDGE,"E106.MirrorCS"),sQuery(id+"F2.wireOp",EDGE,"E107.MirrorCS"),sQuery(id+"F2.wireOp",EDGE,"E108.MirrorCS"),sQuery(id+"F2.wireOp",EDGE,"E116.MirrorCS"),sQuery(id+"F2.wireOp",EDGE,"E118.MirrorCS"),sQuery(id+"F2.wireOp",EDGE,"E119.MirrorCS"),sQuery(id+"F2.wireOp",EDGE,"E121.MirrorCS"),sQuery(id+"F2.wireOp",EDGE,"E122.MirrorCS"),sQuery(id+"F2.wireOp",EDGE,"E128.MirrorCS"),sQuery(id+"F2.wireOp",EDGE,"E112.MirrorCS"),sQuery(id+"F2.wireOp",EDGE,"E130.MirrorCS"),sQuery(id+"F2.wireOp",EDGE,"E131.MirrorCS"),sQuery(id+"F2.wireOp",EDGE,"E132.MirrorCS"),sQuery(id+"F2.wireOp",EDGE,"E134"),sQuery(id+"F2.wireOp",EDGE,"E135.MirrorCS"),sQuery(id+"F2.wireOp",EDGE,"E136.trimOffspring"),sQuery(id+"F2.wireOp",EDGE,"E138.MirrorCS"),sQuery(id+"F2.wireOp",EDGE,"E139.MirrorCS"),sQuery(id+"F2.wireOp",EDGE,"E140.trimOffspring"),sQuery(id+"F2.wireOp",EDGE,"E141.trimOffspring"),sQuery(id+"F2.wireOp",EDGE,"E142.trimOffspring")])]}),"instanceName":"1"});
            var Q1;
            Q1=makeQuery(id+"F1.opExtrude","SWEPT_BODY",BODY,{"disambiguationData":[OSD([sQuery(id+"F0.wireOp",EDGE,"E0.bottom"),sQuery(id+"F0.wireOp",EDGE,"E0.top"),sQuery(id+"F0.wireOp",EDGE,"E0.left"),sQuery(id+"F0.wireOp",EDGE,"E0.right"),sQuery(id+"F0.wireOp",EDGE,"E3.trimOffspring"),sQuery(id+"F0.wireOp",EDGE,"E6.bottom"),sQuery(id+"F0.wireOp",EDGE,"E6.top"),sQuery(id+"F0.wireOp",EDGE,"E6.left"),sQuery(id+"F0.wireOp",EDGE,"E6.right"),sQuery(id+"F0.wireOp",EDGE,"E7.bottom"),sQuery(id+"F0.wireOp",EDGE,"E7.top"),sQuery(id+"F0.wireOp",EDGE,"E7.left"),sQuery(id+"F0.wireOp",EDGE,"E7.right"),sQuery(id+"F0.wireOp",EDGE,"E10"),sQuery(id+"F0.wireOp",EDGE,"E14.MirrorCS"),sQuery(id+"F0.wireOp",EDGE,"E15.MirrorCS"),sQuery(id+"F0.wireOp",EDGE,"E11.MirrorCS"),sQuery(id+"F0.wireOp",EDGE,"E16.MirrorCS"),sQuery(id+"F0.wireOp",EDGE,"E17.MirrorC"),sQuery(id+"F0.wireOp",EDGE,"E18.MirrorCS"),sQuery(id+"F0.wireOp",EDGE,"E19.MirrorCS"),sQuery(id+"F0.wireOp",EDGE,"E22.MirrorCS"),sQuery(id+"F0.wireOp",EDGE,"E23.MirrorCS"),sQuery(id+"F0.wireOp",EDGE,"E28.MirrorCS"),sQuery(id+"F0.wireOp",EDGE,"E29.MirrorCS"),sQuery(id+"F0.wireOp",EDGE,"E30.MirrorCS"),sQuery(id+"F0.wireOp",EDGE,"E31.MirrorCS"),sQuery(id+"F0.wireOp",EDGE,"E32.MirrorC"),sQuery(id+"F0.wireOp",EDGE,"E33.MirrorCS"),sQuery(id+"F0.wireOp",EDGE,"E34.MirrorCS"),sQuery(id+"F0.wireOp",EDGE,"E35.MirrorCS"),sQuery(id+"F0.wireOp",EDGE,"E36.MirrorCS"),sQuery(id+"F0.wireOp",EDGE,"E37.MirrorCS"),sQuery(id+"F0.wireOp",EDGE,"E38.MirrorCS"),sQuery(id+"F0.wireOp",EDGE,"E39.MirrorCS"),sQuery(id+"F0.wireOp",EDGE,"E40.MirrorCS"),sQuery(id+"F0.wireOp",EDGE,"E41.MirrorC"),sQuery(id+"F0.wireOp",EDGE,"E42.MirrorCS"),sQuery(id+"F0.wireOp",EDGE,"E43.MirrorCS"),sQuery(id+"F0.wireOp",EDGE,"E44.MirrorCS"),sQuery(id+"F0.wireOp",EDGE,"E45.MirrorCS"),sQuery(id+"F0.wireOp",EDGE,"E46.left"),sQuery(id+"F0.wireOp",EDGE,"E46.right"),sQuery(id+"F0.wireOp",EDGE,"E47")])]});
            var Q2;
            Q2=makeQuery(id+"F5.opPattern","COPY",FACE,{"derivedFrom":makeQuery(id+"F3.opExtrude","CAP_FACE",FACE,{"disambiguationData":[OSD([sQuery(id+"F2.wireOp",EDGE,"E49.bottom"),sQuery(id+"F2.wireOp",EDGE,"E49.top"),sQuery(id+"F2.wireOp",EDGE,"E50.bottom"),sQuery(id+"F2.wireOp",EDGE,"E50.top"),sQuery(id+"F2.wireOp",EDGE,"E50.right"),sQuery(id+"F2.wireOp",EDGE,"E51.bottom"),sQuery(id+"F2.wireOp",EDGE,"E51.top"),sQuery(id+"F2.wireOp",EDGE,"E51.left"),sQuery(id+"F2.wireOp",EDGE,"E51.right"),sQuery(id+"F2.wireOp",EDGE,"E52.bottom"),sQuery(id+"F2.wireOp",EDGE,"E52.top"),sQuery(id+"F2.wireOp",EDGE,"E52.right"),sQuery(id+"F2.wireOp",EDGE,"E53.bottom"),sQuery(id+"F2.wireOp",EDGE,"E53.top"),sQuery(id+"F2.wireOp",EDGE,"E53.left"),sQuery(id+"F2.wireOp",EDGE,"E53.right"),sQuery(id+"F2.wireOp",EDGE,"E54.trimOffspring"),sQuery(id+"F2.wireOp",EDGE,"E55.trimOffspring"),sQuery(id+"F2.wireOp",EDGE,"E56.trimOffspring"),sQuery(id+"F2.wireOp",EDGE,"E57.trimOffspring"),sQuery(id+"F2.wireOp",EDGE,"E58.trimOffspring"),sQuery(id+"F2.wireOp",EDGE,"E59.trimOffspring"),sQuery(id+"F2.wireOp",EDGE,"E60.trimOffspring"),sQuery(id+"F2.wireOp",EDGE,"E61.trimOffspring"),sQuery(id+"F2.wireOp",EDGE,"E63.bottom"),sQuery(id+"F2.wireOp",EDGE,"E63.left"),sQuery(id+"F2.wireOp",EDGE,"E64.top"),sQuery(id+"F2.wireOp",EDGE,"E66.bottom"),sQuery(id+"F2.wireOp",EDGE,"E66.top"),sQuery(id+"F2.wireOp",EDGE,"E66.right"),sQuery(id+"F2.wireOp",EDGE,"E67"),sQuery(id+"F2.wireOp",EDGE,"E68"),sQuery(id+"F2.wireOp",EDGE,"E69"),sQuery(id+"F2.wireOp",EDGE,"E70.trimOffspring"),sQuery(id+"F2.wireOp",EDGE,"E71.trimOffspring"),sQuery(id+"F2.wireOp",EDGE,"E72"),sQuery(id+"F2.wireOp",EDGE,"E73"),sQuery(id+"F2.wireOp",EDGE,"E74"),sQuery(id+"F2.wireOp",EDGE,"E76"),sQuery(id+"F2.wireOp",EDGE,"E77.trimOffspring"),sQuery(id+"F2.wireOp",EDGE,"E49.left"),sQuery(id+"F2.wireOp",EDGE,"E78"),sQuery(id+"F2.wireOp",EDGE,"E79.trimOffspring"),sQuery(id+"F2.wireOp",EDGE,"E81.MirrorCS"),sQuery(id+"F2.wireOp",EDGE,"E83.MirrorCS"),sQuery(id+"F2.wireOp",EDGE,"E84.MirrorCS"),sQuery(id+"F2.wireOp",EDGE,"E85.MirrorCS"),sQuery(id+"F2.wireOp",EDGE,"E86.MirrorCS"),sQuery(id+"F2.wireOp",EDGE,"E87.MirrorCS"),sQuery(id+"F2.wireOp",EDGE,"E88.MirrorCS"),sQuery(id+"F2.wireOp",EDGE,"E89.MirrorCS"),sQuery(id+"F2.wireOp",EDGE,"E90.MirrorCS"),sQuery(id+"F2.wireOp",EDGE,"E91.MirrorCS"),sQuery(id+"F2.wireOp",EDGE,"E92.MirrorCS"),sQuery(id+"F2.wireOp",EDGE,"E93.MirrorCS"),sQuery(id+"F2.wireOp",EDGE,"E94.MirrorCS"),sQuery(id+"F2.wireOp",EDGE,"E95.MirrorCS"),sQuery(id+"F2.wireOp",EDGE,"E96.MirrorCS"),sQuery(id+"F2.wireOp",EDGE,"E97.MirrorCS"),sQuery(id+"F2.wireOp",EDGE,"E98.MirrorCS"),sQuery(id+"F2.wireOp",EDGE,"E99.MirrorCS"),sQuery(id+"F2.wireOp",EDGE,"E100.MirrorCS"),sQuery(id+"F2.wireOp",EDGE,"E101.MirrorCS"),sQuery(id+"F2.wireOp",EDGE,"E102.MirrorCS"),sQuery(id+"F2.wireOp",EDGE,"E104.MirrorCS"),sQuery(id+"F2.wireOp",EDGE,"E105.MirrorCS"),sQuery(id+"F2.wireOp",EDGE,"E106.MirrorCS"),sQuery(id+"F2.wireOp",EDGE,"E107.MirrorCS"),sQuery(id+"F2.wireOp",EDGE,"E108.MirrorCS"),sQuery(id+"F2.wireOp",EDGE,"E116.MirrorCS"),sQuery(id+"F2.wireOp",EDGE,"E118.MirrorCS"),sQuery(id+"F2.wireOp",EDGE,"E119.MirrorCS"),sQuery(id+"F2.wireOp",EDGE,"E121.MirrorCS"),sQuery(id+"F2.wireOp",EDGE,"E122.MirrorCS"),sQuery(id+"F2.wireOp",EDGE,"E128.MirrorCS"),sQuery(id+"F2.wireOp",EDGE,"E112.MirrorCS"),sQuery(id+"F2.wireOp",EDGE,"E130.MirrorCS"),sQuery(id+"F2.wireOp",EDGE,"E131.MirrorCS"),sQuery(id+"F2.wireOp",EDGE,"E132.MirrorCS"),sQuery(id+"F2.wireOp",EDGE,"E134"),sQuery(id+"F2.wireOp",EDGE,"E135.MirrorCS"),sQuery(id+"F2.wireOp",EDGE,"E136.trimOffspring"),sQuery(id+"F2.wireOp",EDGE,"E138.MirrorCS"),sQuery(id+"F2.wireOp",EDGE,"E139.MirrorCS"),sQuery(id+"F2.wireOp",EDGE,"E140.trimOffspring"),sQuery(id+"F2.wireOp",EDGE,"E141.trimOffspring"),sQuery(id+"F2.wireOp",EDGE,"E142.trimOffspring")])],"isStart":true}),"instanceName":"1"});
            var Q3;
            Q3=makeQuery(id+"F5.opPattern","COPY",FACE,{"derivedFrom":makeQuery(id+"F3.opExtrude","CAP_FACE",FACE,{"disambiguationData":[OSD([sQuery(id+"F2.wireOp",EDGE,"E49.bottom"),sQuery(id+"F2.wireOp",EDGE,"E49.top"),sQuery(id+"F2.wireOp",EDGE,"E50.bottom"),sQuery(id+"F2.wireOp",EDGE,"E50.top"),sQuery(id+"F2.wireOp",EDGE,"E50.right"),sQuery(id+"F2.wireOp",EDGE,"E51.bottom"),sQuery(id+"F2.wireOp",EDGE,"E51.top"),sQuery(id+"F2.wireOp",EDGE,"E51.left"),sQuery(id+"F2.wireOp",EDGE,"E51.right"),sQuery(id+"F2.wireOp",EDGE,"E52.bottom"),sQuery(id+"F2.wireOp",EDGE,"E52.top"),sQuery(id+"F2.wireOp",EDGE,"E52.right"),sQuery(id+"F2.wireOp",EDGE,"E53.bottom"),sQuery(id+"F2.wireOp",EDGE,"E53.top"),sQuery(id+"F2.wireOp",EDGE,"E53.left"),sQuery(id+"F2.wireOp",EDGE,"E53.right"),sQuery(id+"F2.wireOp",EDGE,"E54.trimOffspring"),sQuery(id+"F2.wireOp",EDGE,"E55.trimOffspring"),sQuery(id+"F2.wireOp",EDGE,"E56.trimOffspring"),sQuery(id+"F2.wireOp",EDGE,"E57.trimOffspring"),sQuery(id+"F2.wireOp",EDGE,"E58.trimOffspring"),sQuery(id+"F2.wireOp",EDGE,"E59.trimOffspring"),sQuery(id+"F2.wireOp",EDGE,"E60.trimOffspring"),sQuery(id+"F2.wireOp",EDGE,"E61.trimOffspring"),sQuery(id+"F2.wireOp",EDGE,"E63.bottom"),sQuery(id+"F2.wireOp",EDGE,"E63.left"),sQuery(id+"F2.wireOp",EDGE,"E64.top"),sQuery(id+"F2.wireOp",EDGE,"E66.bottom"),sQuery(id+"F2.wireOp",EDGE,"E66.top"),sQuery(id+"F2.wireOp",EDGE,"E66.right"),sQuery(id+"F2.wireOp",EDGE,"E67"),sQuery(id+"F2.wireOp",EDGE,"E68"),sQuery(id+"F2.wireOp",EDGE,"E69"),sQuery(id+"F2.wireOp",EDGE,"E70.trimOffspring"),sQuery(id+"F2.wireOp",EDGE,"E71.trimOffspring"),sQuery(id+"F2.wireOp",EDGE,"E72"),sQuery(id+"F2.wireOp",EDGE,"E73"),sQuery(id+"F2.wireOp",EDGE,"E74"),sQuery(id+"F2.wireOp",EDGE,"E76"),sQuery(id+"F2.wireOp",EDGE,"E77.trimOffspring"),sQuery(id+"F2.wireOp",EDGE,"E49.left"),sQuery(id+"F2.wireOp",EDGE,"E78"),sQuery(id+"F2.wireOp",EDGE,"E79.trimOffspring"),sQuery(id+"F2.wireOp",EDGE,"E81.MirrorCS"),sQuery(id+"F2.wireOp",EDGE,"E83.MirrorCS"),sQuery(id+"F2.wireOp",EDGE,"E84.MirrorCS"),sQuery(id+"F2.wireOp",EDGE,"E85.MirrorCS"),sQuery(id+"F2.wireOp",EDGE,"E86.MirrorCS"),sQuery(id+"F2.wireOp",EDGE,"E87.MirrorCS"),sQuery(id+"F2.wireOp",EDGE,"E88.MirrorCS"),sQuery(id+"F2.wireOp",EDGE,"E89.MirrorCS"),sQuery(id+"F2.wireOp",EDGE,"E90.MirrorCS"),sQuery(id+"F2.wireOp",EDGE,"E91.MirrorCS"),sQuery(id+"F2.wireOp",EDGE,"E92.MirrorCS"),sQuery(id+"F2.wireOp",EDGE,"E93.MirrorCS"),sQuery(id+"F2.wireOp",EDGE,"E94.MirrorCS"),sQuery(id+"F2.wireOp",EDGE,"E95.MirrorCS"),sQuery(id+"F2.wireOp",EDGE,"E96.MirrorCS"),sQuery(id+"F2.wireOp",EDGE,"E97.MirrorCS"),sQuery(id+"F2.wireOp",EDGE,"E98.MirrorCS"),sQuery(id+"F2.wireOp",EDGE,"E99.MirrorCS"),sQuery(id+"F2.wireOp",EDGE,"E100.MirrorCS"),sQuery(id+"F2.wireOp",EDGE,"E101.MirrorCS"),sQuery(id+"F2.wireOp",EDGE,"E102.MirrorCS"),sQuery(id+"F2.wireOp",EDGE,"E104.MirrorCS"),sQuery(id+"F2.wireOp",EDGE,"E105.MirrorCS"),sQuery(id+"F2.wireOp",EDGE,"E106.MirrorCS"),sQuery(id+"F2.wireOp",EDGE,"E107.MirrorCS"),sQuery(id+"F2.wireOp",EDGE,"E108.MirrorCS"),sQuery(id+"F2.wireOp",EDGE,"E116.MirrorCS"),sQuery(id+"F2.wireOp",EDGE,"E118.MirrorCS"),sQuery(id+"F2.wireOp",EDGE,"E119.MirrorCS"),sQuery(id+"F2.wireOp",EDGE,"E121.MirrorCS"),sQuery(id+"F2.wireOp",EDGE,"E122.MirrorCS"),sQuery(id+"F2.wireOp",EDGE,"E128.MirrorCS"),sQuery(id+"F2.wireOp",EDGE,"E112.MirrorCS"),sQuery(id+"F2.wireOp",EDGE,"E130.MirrorCS"),sQuery(id+"F2.wireOp",EDGE,"E131.MirrorCS"),sQuery(id+"F2.wireOp",EDGE,"E132.MirrorCS"),sQuery(id+"F2.wireOp",EDGE,"E134"),sQuery(id+"F2.wireOp",EDGE,"E135.MirrorCS"),sQuery(id+"F2.wireOp",EDGE,"E136.trimOffspring"),sQuery(id+"F2.wireOp",EDGE,"E138.MirrorCS"),sQuery(id+"F2.wireOp",EDGE,"E139.MirrorCS"),sQuery(id+"F2.wireOp",EDGE,"E140.trimOffspring"),sQuery(id+"F2.wireOp",EDGE,"E141.trimOffspring"),sQuery(id+"F2.wireOp",EDGE,"E142.trimOffspring")])],"isStart":false}),"instanceName":"1"});
            var Q4;
            Q4=makeQuery(id+"F5.opPattern","COPY",FACE,{"derivedFrom":makeQuery(id+"F3.opExtrude","SWEPT_FACE",FACE,{"disambiguationData":[OSD([sQuery(id+"F2.wireOp",EDGE,"E63.bottom")])]}),"instanceName":"1"});
            var Q5;
            Q5=makeQuery(id+"F5.opPattern","COPY",FACE,{"derivedFrom":makeQuery(id+"F3.opExtrude","SWEPT_FACE",FACE,{"disambiguationData":[OSD([sQuery(id+"F2.wireOp",EDGE,"E64.top")])]}),"instanceName":"1"});
            var Q6;
            Q6=makeQuery(id+"F5.opPattern","COPY",FACE,{"derivedFrom":makeQuery(id+"F3.opExtrude","SWEPT_FACE",FACE,{"disambiguationData":[OSD([sQuery(id+"F2.wireOp",EDGE,"E66.bottom")])]}),"instanceName":"1"});
            var Q7;
            Q7=makeQuery(id+"F5.opPattern","COPY",FACE,{"derivedFrom":makeQuery(id+"F3.opExtrude","SWEPT_FACE",FACE,{"disambiguationData":[OSD([sQuery(id+"F2.wireOp",EDGE,"E69")])]}),"instanceName":"1"});
            var Q8;
            Q8=makeQuery(id+"F5.opPattern","COPY",FACE,{"derivedFrom":makeQuery(id+"F3.opExtrude","SWEPT_FACE",FACE,{"disambiguationData":[OSD([sQuery(id+"F2.wireOp",EDGE,"E68")])]}),"instanceName":"1"});
            var Q9;
            Q9=makeQuery(id+"F5.opPattern","COPY",FACE,{"derivedFrom":makeQuery(id+"F3.opExtrude","SWEPT_FACE",FACE,{"disambiguationData":[OSD([sQuery(id+"F2.wireOp",EDGE,"E70.trimOffspring")])]}),"instanceName":"1"});
            var Q10;
            Q10=makeQuery(id+"F5.opPattern","COPY",FACE,{"derivedFrom":makeQuery(id+"F3.opExtrude","SWEPT_FACE",FACE,{"disambiguationData":[OSD([sQuery(id+"F2.wireOp",EDGE,"E66.top")])]}),"instanceName":"1"});
            var Q11;
            Q11=makeQuery(id+"F5.opPattern","COPY",FACE,{"derivedFrom":makeQuery(id+"F3.opExtrude","SWEPT_FACE",FACE,{"disambiguationData":[OSD([sQuery(id+"F2.wireOp",EDGE,"E78")])]}),"instanceName":"1"});
            booleanBodies(context, id + "F6", {"operationType" : BooleanOperationType.SUBTRACTION, "tools" : qUnion([Q0]), "targets" : qUnion([Q1]), "offset" : true, "entitiesToOffset" : qUnion([Q2, Q3, Q4, Q5, Q6, Q7, Q8, Q9, Q10, Q11]), "offsetDistance" : 0.6 * mm, "keepTools" : true});
        }
        {
            var Q0;
            Q0=makeQuery(id+"F1.opExtrude","SWEPT_BODY",BODY,{"disambiguationData":[OSD([sQuery(id+"F0.wireOp",EDGE,"E0.bottom"),sQuery(id+"F0.wireOp",EDGE,"E0.top"),sQuery(id+"F0.wireOp",EDGE,"E0.left"),sQuery(id+"F0.wireOp",EDGE,"E0.right"),sQuery(id+"F0.wireOp",EDGE,"E3.trimOffspring"),sQuery(id+"F0.wireOp",EDGE,"E6.bottom"),sQuery(id+"F0.wireOp",EDGE,"E6.top"),sQuery(id+"F0.wireOp",EDGE,"E6.left"),sQuery(id+"F0.wireOp",EDGE,"E6.right"),sQuery(id+"F0.wireOp",EDGE,"E7.bottom"),sQuery(id+"F0.wireOp",EDGE,"E7.top"),sQuery(id+"F0.wireOp",EDGE,"E7.left"),sQuery(id+"F0.wireOp",EDGE,"E7.right"),sQuery(id+"F0.wireOp",EDGE,"E10"),sQuery(id+"F0.wireOp",EDGE,"E14.MirrorCS"),sQuery(id+"F0.wireOp",EDGE,"E15.MirrorCS"),sQuery(id+"F0.wireOp",EDGE,"E11.MirrorCS"),sQuery(id+"F0.wireOp",EDGE,"E16.MirrorCS"),sQuery(id+"F0.wireOp",EDGE,"E17.MirrorC"),sQuery(id+"F0.wireOp",EDGE,"E18.MirrorCS"),sQuery(id+"F0.wireOp",EDGE,"E19.MirrorCS"),sQuery(id+"F0.wireOp",EDGE,"E22.MirrorCS"),sQuery(id+"F0.wireOp",EDGE,"E23.MirrorCS"),sQuery(id+"F0.wireOp",EDGE,"E28.MirrorCS"),sQuery(id+"F0.wireOp",EDGE,"E29.MirrorCS"),sQuery(id+"F0.wireOp",EDGE,"E30.MirrorCS"),sQuery(id+"F0.wireOp",EDGE,"E31.MirrorCS"),sQuery(id+"F0.wireOp",EDGE,"E32.MirrorC"),sQuery(id+"F0.wireOp",EDGE,"E33.MirrorCS"),sQuery(id+"F0.wireOp",EDGE,"E34.MirrorCS"),sQuery(id+"F0.wireOp",EDGE,"E35.MirrorCS"),sQuery(id+"F0.wireOp",EDGE,"E36.MirrorCS"),sQuery(id+"F0.wireOp",EDGE,"E37.MirrorCS"),sQuery(id+"F0.wireOp",EDGE,"E38.MirrorCS"),sQuery(id+"F0.wireOp",EDGE,"E39.MirrorCS"),sQuery(id+"F0.wireOp",EDGE,"E40.MirrorCS"),sQuery(id+"F0.wireOp",EDGE,"E41.MirrorC"),sQuery(id+"F0.wireOp",EDGE,"E42.MirrorCS"),sQuery(id+"F0.wireOp",EDGE,"E43.MirrorCS"),sQuery(id+"F0.wireOp",EDGE,"E44.MirrorCS"),sQuery(id+"F0.wireOp",EDGE,"E45.MirrorCS"),sQuery(id+"F0.wireOp",EDGE,"E46.left"),sQuery(id+"F0.wireOp",EDGE,"E46.right"),sQuery(id+"F0.wireOp",EDGE,"E47")])]});
            transform(context, id + "F7", {"entities" : qUnion([Q0]), "transformType" : TransformType.TRANSLATION_3D, "dx" : -205 * mm, "dy" : 0 * mm, "dz" : 0 * mm, "makeCopy" : true});
        }
    });
